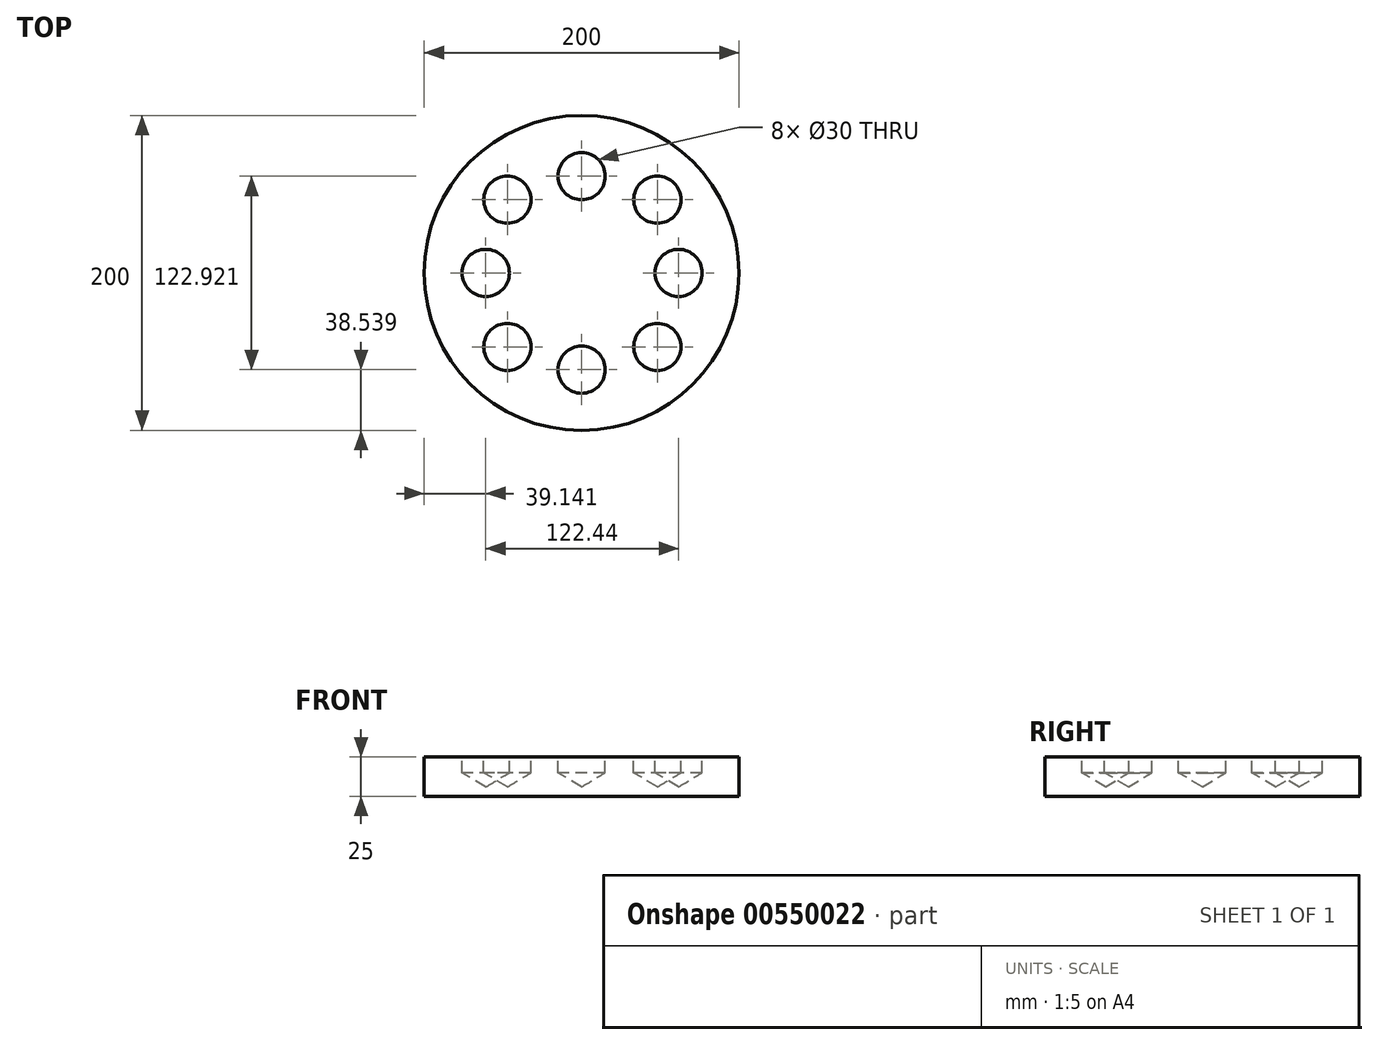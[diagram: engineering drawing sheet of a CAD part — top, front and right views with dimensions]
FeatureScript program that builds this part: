
annotation { "Feature Type Name" : "Feature", "Feature Type Description" : "" }
export const myFeature = defineFeature(function(context is Context, id is Id, definition is map)
    precondition{}
    {
        {
            var Q0;
            Q0=qCreatedBy(makeId("Top.planeOp"),FACE);
            var sketch = newSketch(context, id + "F0", { "sketchPlane" : qUnion([Q0])});
            skCircle(sketch, "E0", {"center": v(0, 0) * mm, "radius": 100 * mm});
            skSolve(sketch);
        }
        {
            var Q0;
            Q0=makeQuery(id+"F0.imprint","IMPRINT",FACE,{"disambiguationData":[TD([[makeQuery(id+"F0.imprint","IMPRINT",EDGE,{"derivedFrom":sQuery(id+"F0.wireOp",EDGE,"E0")}),1.0]])]});
            extrude(context, id + "F1", {"entities" : qUnion([Q0]), "depth" : 25 * mm, "offsetDistance" : 25.4 * mm});
        }
        {
            var Q0;
            Q0=makeQuery(id+"F1.opExtrude","CAP_FACE",FACE,{"disambiguationData":[OSD([sQuery(id+"F0.wireOp",EDGE,"E0")])],"isStart":false});
            var sketch = newSketch(context, id + "F2", { "sketchPlane" : qUnion([Q0])});
            skCircle(sketch, "E1", {"center": v(-60.86, 0) * mm, "radius": 15 * mm});
            skCircle(sketch, "E2", {"center": v(0, 61.46) * mm, "radius": 15 * mm});
            skCircle(sketch, "E3", {"center": v(0, -61.46) * mm, "radius": 15 * mm});
            skCircle(sketch, "E4", {"center": v(61.58, 0) * mm, "radius": 15 * mm});
            skCircle(sketch, "E5", {"center": v(-47.15, -47.03) * mm, "radius": 15 * mm});
            skCircle(sketch, "E6", {"center": v(48.1, -47.03) * mm, "radius": 15 * mm});
            skCircle(sketch, "E7", {"center": v(48.1, 46.55) * mm, "radius": 15 * mm});
            skCircle(sketch, "E8", {"center": v(-47.15, 46.55) * mm, "radius": 15 * mm});
            skSolve(sketch);
        }
        {
            var Q0;
            Q0=sQuery(id+"F2.wireOp",VERTEX,"E8.center");
            var Q1;
            Q1=sQuery(id+"F2.wireOp",VERTEX,"E1.center");
            var Q2;
            Q2=sQuery(id+"F2.wireOp",VERTEX,"E5.center");
            var Q3;
            Q3=sQuery(id+"F2.wireOp",VERTEX,"E3.center");
            var Q4;
            Q4=sQuery(id+"F2.wireOp",VERTEX,"E6.center");
            var Q5;
            Q5=sQuery(id+"F2.wireOp",VERTEX,"E4.center");
            var Q6;
            Q6=sQuery(id+"F2.wireOp",VERTEX,"E7.center");
            var Q7;
            Q7=sQuery(id+"F2.wireOp",VERTEX,"E2.center");
            var Q8;
            Q8=makeQuery(id+"F1.opExtrude","SWEPT_BODY",BODY,{"disambiguationData":[OSD([sQuery(id+"F0.wireOp",EDGE,"E0")])]});
            hole(context, id + "F3", {"style" : HoleStyle.SIMPLE, "endStyle" : HoleEndStyle.BLIND, "holeDiameter" : 30 * mm, "holeDepth" : 10 * mm, "isTappedThrough" : true, "tappedDepth" : 12.7 * mm, "tapClearance" : 3, "locations" : qUnion([Q0, Q1, Q2, Q3, Q4, Q5, Q6, Q7]), "scope" : qUnion([Q8])});
        }
    });
